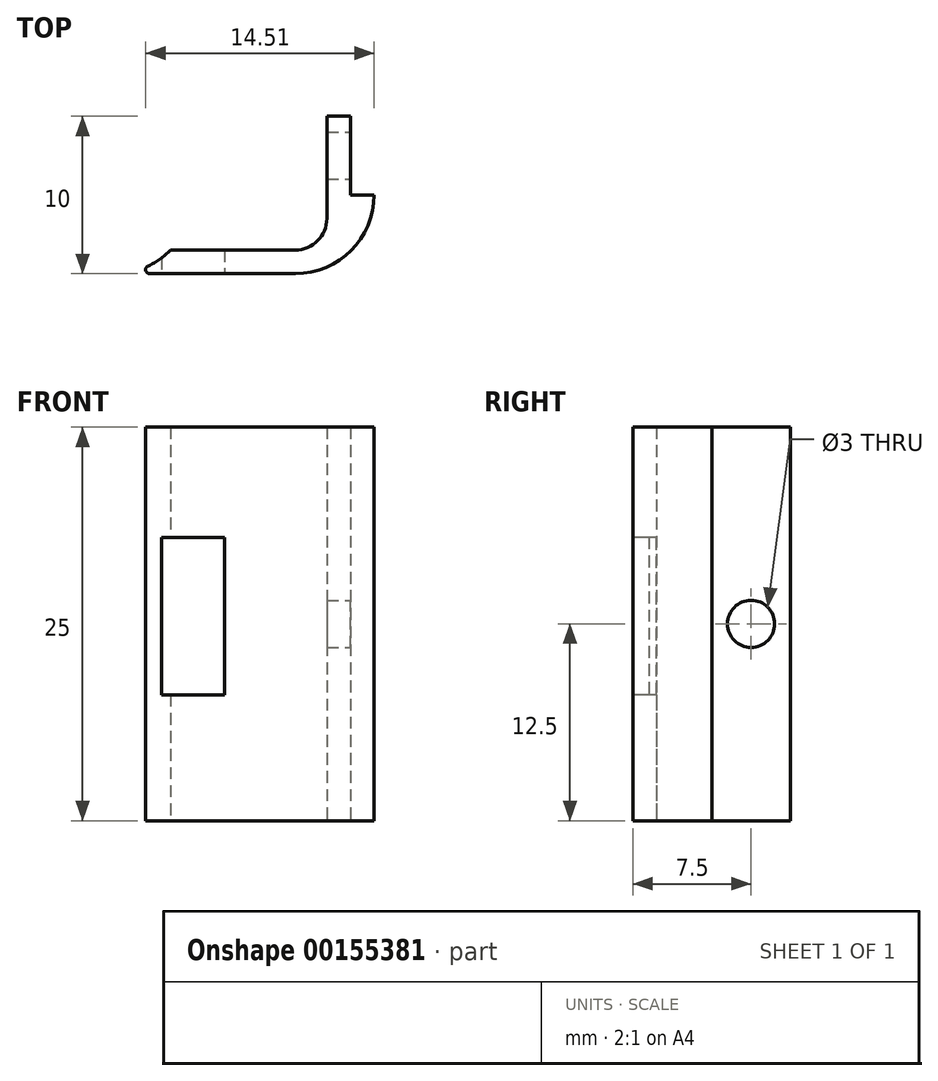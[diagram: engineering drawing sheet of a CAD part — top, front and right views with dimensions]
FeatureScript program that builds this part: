
annotation { "Feature Type Name" : "Feature", "Feature Type Description" : "" }
export const myFeature = defineFeature(function(context is Context, id is Id, definition is map)
    precondition{}
    {
        {
            var Q0;
            Q0=qCreatedBy(makeId("Top.planeOp"),FACE);
            var sketch = newSketch(context, id + "F0", { "sketchPlane" : qUnion([Q0])});
            skLineSegment(sketch, "E0", {"start": v(0, 0) * mm, "end": v(11.5, 0) * mm});
            skArc(sketch, "E1.filletArc", {"start": v(11.5, 0) * mm, "mid": v(15.04, 1.46) * mm, "end": v(16.5, 5) * mm});
            skLineSegment(sketch, "E2.1", {"start": v(0, 1.5) * mm, "end": v(10, 1.5) * mm});
            skLineSegment(sketch, "E3", {"start": v(0, 1.5) * mm, "end": v(0, 0) * mm});
            skCircle(sketch, "E4", {"center": v(0, 5) * mm, "radius": 5 * mm, "construction": true});
            skLineSegment(sketch, "E5", {"start": v(0, 1.5) * mm, "end": v(0, 8.16) * mm, "construction": true});
            skPoint(sketch, "E6", {"position": v(3.57, 1.5) * mm});
            skArc(sketch, "E7", {"start": v(0, 0) * mm, "mid": v(1.94, 0.4) * mm, "end": v(3.57, 1.5) * mm});
            skLineSegment(sketch, "E8", {"start": v(16.5, 5) * mm, "end": v(15, 5) * mm});
            skLineSegment(sketch, "E9", {"start": v(15, 5) * mm, "end": v(13.5, 5) * mm});
            skLineSegment(sketch, "E10", {"start": v(13.5, 5) * mm, "end": v(13.5, 10) * mm});
            skLineSegment(sketch, "E11", {"start": v(13.5, 10) * mm, "end": v(15, 10) * mm});
            skLineSegment(sketch, "E12", {"start": v(15, 10) * mm, "end": v(15, 5) * mm});
            skLineSegment(sketch, "E13", {"start": v(10, 1.5) * mm, "end": v(11.5, 1.5) * mm});
            skLineSegment(sketch, "E14", {"start": v(13.5, 3.5) * mm, "end": v(13.5, 5) * mm});
            skPoint(sketch, "E15.visualSharp", {"position": v(13.5, 1.5) * mm});
            skArc(sketch, "E15.filletArc", {"start": v(11.5, 1.5) * mm, "mid": v(12.91, 2.09) * mm, "end": v(13.5, 3.5) * mm});
            skSolve(sketch);
        }
        {
            var Q0;
            Q0=makeQuery(id+"F0.imprint","IMPRINT",FACE,{"disambiguationData":[TD([[makeQuery(id+"F0.imprint","IMPRINT",EDGE,{"derivedFrom":sQuery(id+"F0.wireOp",EDGE,"E0")}),1.0]])]});
            var Q1;
            Q1=makeQuery(id+"F0.imprint","IMPRINT",FACE,{"disambiguationData":[TD([[makeQuery(id+"F0.imprint","IMPRINT",EDGE,{"derivedFrom":sQuery(id+"F0.wireOp",EDGE,"E9")}),-1.0]])]});
            extrude(context, id + "F1", {"entities" : qUnion([Q0, Q1]), "depth" : 25 * mm});
        }
        {
            var Q0;
            Q0=makeQuery(id+"F1.opExtrude","SWEPT_FACE",FACE,{"disambiguationData":[OSD([sQuery(id+"F0.wireOp",EDGE,"E12")])]});
            var sketch = newSketch(context, id + "F2", { "sketchPlane" : qUnion([Q0])});
            skCircle(sketch, "E16", {"center": v(7.5, 12.5) * mm, "radius": 1.5 * mm});
            skPoint(sketch, "E17", {"position": v(7.5, 25) * mm});
            skPoint(sketch, "E18", {"position": v(-40.9, 34.48) * mm});
            skLineSegment(sketch, "E19", {"start": v(7.5, 25) * mm, "end": v(7.5, 0) * mm, "construction": true});
            skPoint(sketch, "E20", {"position": v(10, 12.5) * mm});
            skLineSegment(sketch, "E21", {"start": v(10, 12.5) * mm, "end": v(5, 12.5) * mm, "construction": true});
            skSolve(sketch);
        }
        {
            var Q0;
            Q0=makeQuery(id+"F2.imprint","IMPRINT",FACE,{"disambiguationData":[TD([[makeQuery(id+"F2.imprint","IMPRINT",EDGE,{"derivedFrom":sQuery(id+"F2.wireOp",EDGE,"E16")}),1.0]])]});
            extrude(context, id + "F3", {"entities" : qUnion([Q0]), "operationType" : NewBodyOperationType.REMOVE, "oppositeDirection" : true, "depth" : 25 * mm});
        }
        {
            var Q0;
            Q0=makeQuery(id+"F1.opExtrude","SWEPT_FACE",FACE,{"disambiguationData":[OSD([sQuery(id+"F0.wireOp",EDGE,"E0")])]});
            var sketch = newSketch(context, id + "F4", { "sketchPlane" : qUnion([Q0])});
            skLineSegment(sketch, "E22.bottom", {"start": v(3, 18) * mm, "end": v(7, 18) * mm});
            skLineSegment(sketch, "E22.top", {"start": v(3, 8) * mm, "end": v(7, 8) * mm});
            skLineSegment(sketch, "E22.left", {"start": v(3, 18) * mm, "end": v(3, 8) * mm});
            skLineSegment(sketch, "E22.right", {"start": v(7, 18) * mm, "end": v(7, 8) * mm});
            skSolve(sketch);
        }
        {
            var Q0;
            Q0=makeQuery(id+"F4.imprint","IMPRINT",FACE,{"disambiguationData":[TD([[makeQuery(id+"F4.imprint","IMPRINT",EDGE,{"derivedFrom":sQuery(id+"F4.wireOp",EDGE,"E22.bottom")}),-1.0]])]});
            extrude(context, id + "F5", {"entities" : qUnion([Q0]), "operationType" : NewBodyOperationType.REMOVE, "oppositeDirection" : true, "depth" : 25 * mm});
        }
        {
            var Q0;
            Q0=makeQuery(id+"F1.opExtrude","SWEPT_EDGE",EDGE,{"disambiguationData":[OSD([sQuery(id+"F0.wireOp",EDGE,"E0"),sQuery(id+"F0.wireOp",EDGE,"E3"),sQuery(id+"F0.wireOp",EDGE,"E7")])]});
            fillet(context, id + "F6", {"entities" : qUnion([Q0]), "radius" : 0.25 * mm, "tangentPropagation" : true, "allowEdgeOverflow" : false});
        }
    });
